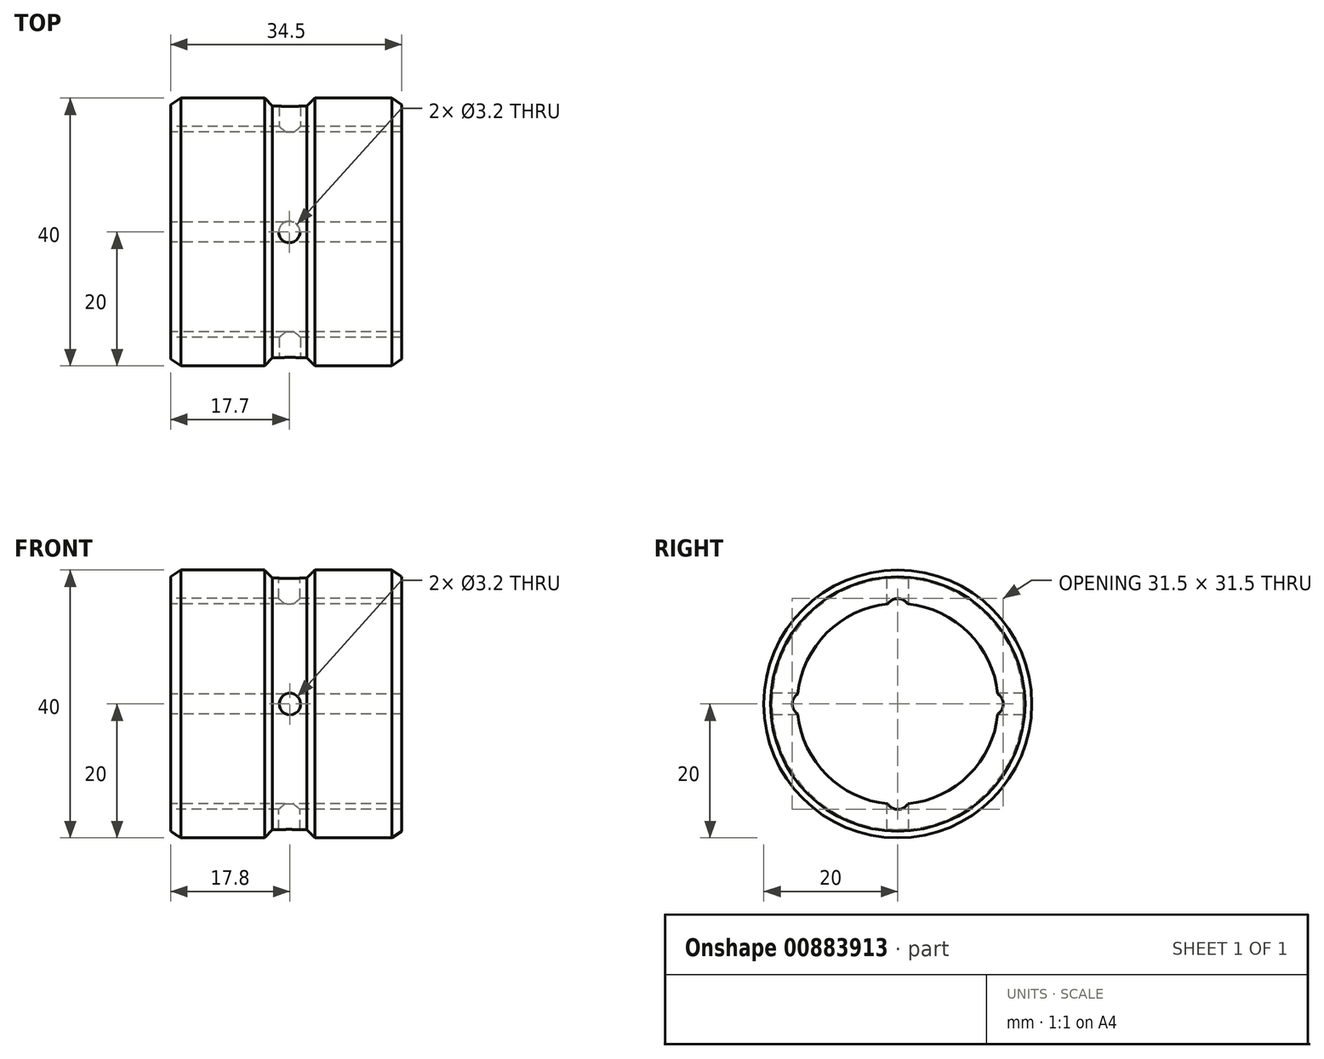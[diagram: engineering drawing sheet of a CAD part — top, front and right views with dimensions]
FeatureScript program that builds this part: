
annotation { "Feature Type Name" : "Feature", "Feature Type Description" : "" }
export const myFeature = defineFeature(function(context is Context, id is Id, definition is map)
    precondition{}
    {
        {
            var Q0;
            Q0=qCreatedBy(makeId("Front.planeOp"),FACE);
            var sketch = newSketch(context, id + "F0", { "sketchPlane" : qUnion([Q0])});
            skLineSegment(sketch, "E0", {"start": v(-55.79, 0) * mm, "end": v(56.64, 0) * mm, "construction": true});
            skLineSegment(sketch, "E1", {"start": v(0, 15) * mm, "end": v(34.5, 15) * mm});
            skLineSegment(sketch, "E2", {"start": v(34.5, 15) * mm, "end": v(34.5, 20) * mm});
            skLineSegment(sketch, "E3", {"start": v(34.5, 20) * mm, "end": v(34.5, 20) * mm});
            skLineSegment(sketch, "E4", {"start": v(34.5, 20) * mm, "end": v(21.5, 20) * mm});
            skLineSegment(sketch, "E5", {"start": v(21.5, 20) * mm, "end": v(20.3, 18.8) * mm});
            skLineSegment(sketch, "E6", {"start": v(20.3, 18.8) * mm, "end": v(15.2, 18.8) * mm});
            skLineSegment(sketch, "E7", {"start": v(15.2, 18.8) * mm, "end": v(14, 20) * mm});
            skLineSegment(sketch, "E8", {"start": v(14, 20) * mm, "end": v(0, 20) * mm});
            skLineSegment(sketch, "E9", {"start": v(0, 20) * mm, "end": v(0, 20) * mm});
            skLineSegment(sketch, "E10", {"start": v(0, 20) * mm, "end": v(0, 15) * mm});
            skSolve(sketch);
        }
        {
            var Q0;
            Q0=makeQuery(id+"F0.imprint","IMPRINT",FACE,{"disambiguationData":[TD([[makeQuery(id+"F0.imprint","IMPRINT",EDGE,{"derivedFrom":sQuery(id+"F0.wireOp",EDGE,"E1")}),1.0]])]});
            var Q1;
            Q1=sQuery(id+"F0.wireOp",EDGE,"E0");
            revolve(context, id + "F1", {"surfaceOperationType" : NewSurfaceOperationType.NEW, "entities" : qUnion([Q0]), "axis" : qUnion([Q1]), "revolveType" : RevolveType.FULL});
        }
        {
            var Q0;
            Q0=qCreatedBy(makeId("Right.planeOp"),FACE);
            var sketch = newSketch(context, id + "F2", { "sketchPlane" : qUnion([Q0])});
            skLineSegment(sketch, "E11", {"start": v(0, 35.5) * mm, "end": v(0, -31.48) * mm, "construction": true});
            skLineSegment(sketch, "E12", {"start": v(38.07, 0) * mm, "end": v(-40.26, 0) * mm, "construction": true});
            skLineSegment(sketch, "E13", {"start": v(-40.26, 0) * mm, "end": v(-40.26, 0.62) * mm, "construction": true});
            skCircle(sketch, "E14", {"center": v(14, 0) * mm, "radius": 1.75 * mm});
            skCircle(sketch, "E15.1.0", {"center": v(0, -14) * mm, "radius": 1.75 * mm});
            skCircle(sketch, "E15.2.0", {"center": v(-14, 0) * mm, "radius": 1.75 * mm});
            skCircle(sketch, "E15.3.0", {"center": v(0, 14) * mm, "radius": 1.75 * mm});
            skPoint(sketch, "E15.center", {"position": v(0, 0) * mm});
            skLineSegment(sketch, "E15.anchor1", {"start": v(0, 0) * mm, "end": v(14, 0) * mm, "construction": true});
            skLineSegment(sketch, "E15.anchor2", {"start": v(0, 0) * mm, "end": v(0, 14) * mm, "construction": true});
            skSolve(sketch);
        }
        {
            var Q0;
            Q0=makeQuery(id+"F2.imprint","IMPRINT",FACE,{"disambiguationData":[TD([[makeQuery(id+"F2.imprint","IMPRINT",EDGE,{"derivedFrom":sQuery(id+"F2.wireOp",EDGE,"E14")}),1.0]])]});
            var Q1;
            Q1=makeQuery(id+"F2.imprint","IMPRINT",FACE,{"disambiguationData":[TD([[makeQuery(id+"F2.imprint","IMPRINT",EDGE,{"derivedFrom":sQuery(id+"F2.wireOp",EDGE,"E15.3.0")}),1.0]])]});
            var Q2;
            Q2=makeQuery(id+"F2.imprint","IMPRINT",FACE,{"disambiguationData":[TD([[makeQuery(id+"F2.imprint","IMPRINT",EDGE,{"derivedFrom":sQuery(id+"F2.wireOp",EDGE,"E15.2.0")}),1.0]])]});
            var Q3;
            Q3=makeQuery(id+"F2.imprint","IMPRINT",FACE,{"disambiguationData":[TD([[makeQuery(id+"F2.imprint","IMPRINT",EDGE,{"derivedFrom":sQuery(id+"F2.wireOp",EDGE,"E15.1.0")}),1.0]])]});
            extrude(context, id + "F3", {"entities" : qUnion([Q0, Q1, Q2, Q3]), "operationType" : NewBodyOperationType.REMOVE, "endBound" : BoundingType.THROUGH_ALL, "depth" : 25 * mm, "offsetDistance" : 25 * mm});
        }
        {
            var Q0;
            Q0=qCreatedBy(makeId("Top.planeOp"),FACE);
            var sketch = newSketch(context, id + "F4", { "sketchPlane" : qUnion([Q0])});
            skLineSegment(sketch, "E16", {"start": v(17.7, -17.13) * mm, "end": v(17.7, 18) * mm, "construction": true});
            skLineSegment(sketch, "E17", {"start": v(17.7, 18) * mm, "end": v(17.3, 18) * mm, "construction": true});
            skCircle(sketch, "E18", {"center": v(17.7, 0) * mm, "radius": 1.6 * mm});
            skSolve(sketch);
        }
        {
            var Q0;
            Q0=makeQuery(id+"F4.imprint","IMPRINT",FACE,{"disambiguationData":[TD([[makeQuery(id+"F4.imprint","IMPRINT",EDGE,{"derivedFrom":sQuery(id+"F4.wireOp",EDGE,"E18")}),1.0]])]});
            extrude(context, id + "F5", {"entities" : qUnion([Q0]), "operationType" : NewBodyOperationType.REMOVE, "endBound" : BoundingType.THROUGH_ALL, "oppositeDirection" : true, "depth" : 25 * mm, "offsetDistance" : 25 * mm, "hasSecondDirection" : true, "secondDirectionBound" : SecondDirectionBoundingType.THROUGH_ALL, "secondDirectionOppositeDirection" : false, "secondDirectionDepth" : 25 * mm});
        }
        {
            var Q0;
            Q0=qCreatedBy(makeId("Front.planeOp"),FACE);
            var sketch = newSketch(context, id + "F6", { "sketchPlane" : qUnion([Q0])});
            skCircle(sketch, "E19", {"center": v(17.8, 0) * mm, "radius": 1.6 * mm});
            skSolve(sketch);
        }
        {
            var Q0;
            Q0=makeQuery(id+"F6.imprint","IMPRINT",FACE,{"disambiguationData":[TD([[makeQuery(id+"F6.imprint","IMPRINT",EDGE,{"derivedFrom":sQuery(id+"F6.wireOp",EDGE,"E19")}),1.0]])]});
            extrude(context, id + "F7", {"entities" : qUnion([Q0]), "operationType" : NewBodyOperationType.REMOVE, "endBound" : BoundingType.THROUGH_ALL, "oppositeDirection" : true, "depth" : 25 * mm, "offsetDistance" : 25 * mm, "hasSecondDirection" : true, "secondDirectionBound" : SecondDirectionBoundingType.THROUGH_ALL, "secondDirectionOppositeDirection" : false, "secondDirectionDepth" : 25 * mm});
        }
        {
            var Q0;
            Q0=makeQuery(id+"F1.opRevolve","SWEPT_EDGE",EDGE,{"disambiguationData":[OSD([sQuery(id+"F0.wireOp",EDGE,"E2"),sQuery(id+"F0.wireOp",EDGE,"E4")])]});
            chamfer(context, id + "F8", {"entities" : qUnion([Q0]), "chamferType" : ChamferType.TWO_OFFSETS, "width1" : 1.5 * mm, "oppositeDirection" : false, "width2" : 1 * mm, "tangentPropagation" : true});
        }
        {
            var Q0;
            Q0=makeQuery(id+"F1.opRevolve","SWEPT_EDGE",EDGE,{"disambiguationData":[OSD([sQuery(id+"F0.wireOp",EDGE,"E8"),sQuery(id+"F0.wireOp",EDGE,"E10")])]});
            chamfer(context, id + "F9", {"entities" : qUnion([Q0]), "chamferType" : ChamferType.TWO_OFFSETS, "width1" : 1 * mm, "oppositeDirection" : false, "width2" : 1.5 * mm, "tangentPropagation" : true});
        }
    });
